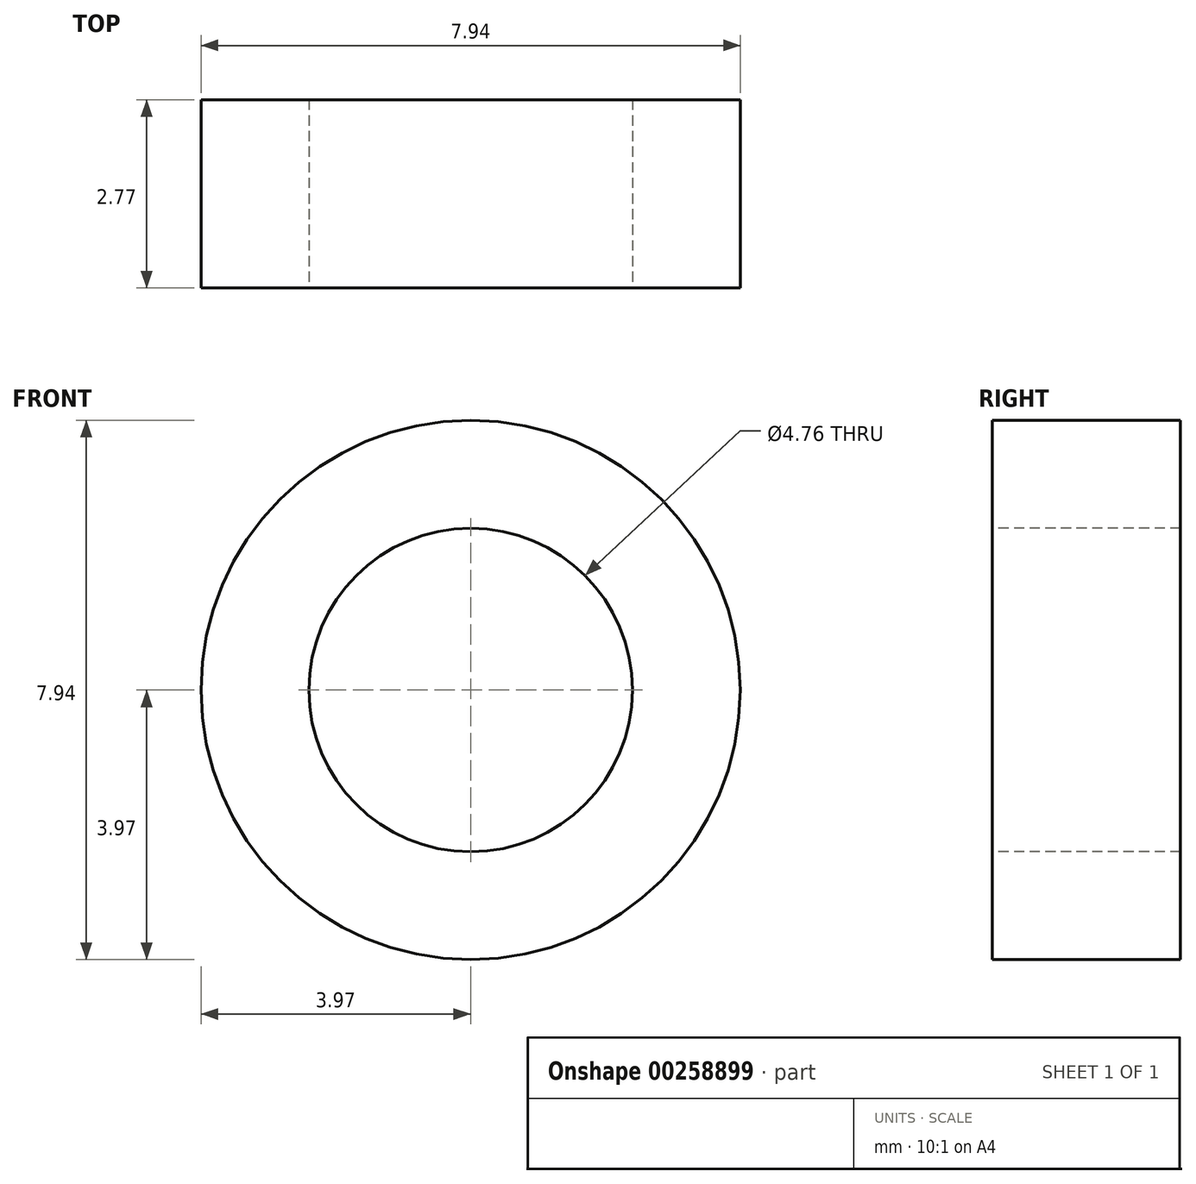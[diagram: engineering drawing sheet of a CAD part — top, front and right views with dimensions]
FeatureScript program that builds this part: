
annotation { "Feature Type Name" : "Feature", "Feature Type Description" : "" }
export const myFeature = defineFeature(function(context is Context, id is Id, definition is map)
    precondition{}
    {
        {
            var Q0;
            Q0=qCreatedBy(makeId("Front.planeOp"),FACE);
            var sketch = newSketch(context, id + "F0", { "sketchPlane" : qUnion([Q0])});
            skCircle(sketch, "E0", {"center": v(0, 0) * mm, "radius": 3.97 * mm});
            skSolve(sketch);
        }
        {
            var Q0;
            Q0=qSketchRegion(id+"F0",true);
            extrude(context, id + "F1", {"entities" : qUnion([Q0]), "depth" : 2.77 * mm});
        }
        {
            var Q0;
            Q0=makeQuery(id+"F1.opExtrude","CAP_FACE",FACE,{"disambiguationData":[OSD([sQuery(id+"F0.wireOp",EDGE,"E0")])],"isStart":false});
            var sketch = newSketch(context, id + "F2", { "sketchPlane" : qUnion([Q0])});
            skCircle(sketch, "E1", {"center": v(0, 0) * mm, "radius": 2.38 * mm});
            skSolve(sketch);
        }
        {
            var Q0;
            Q0=qSketchRegion(id+"F2",true);
            extrude(context, id + "F3", {"entities" : qUnion([Q0]), "operationType" : NewBodyOperationType.REMOVE, "oppositeDirection" : true, "depth" : 25.4 * mm, "hasSecondDirection" : true, "secondDirectionBound" : BoundingType.THROUGH_ALL, "secondDirectionOppositeDirection" : false, "secondDirectionDepth" : 25.4 * mm});
        }
    });
